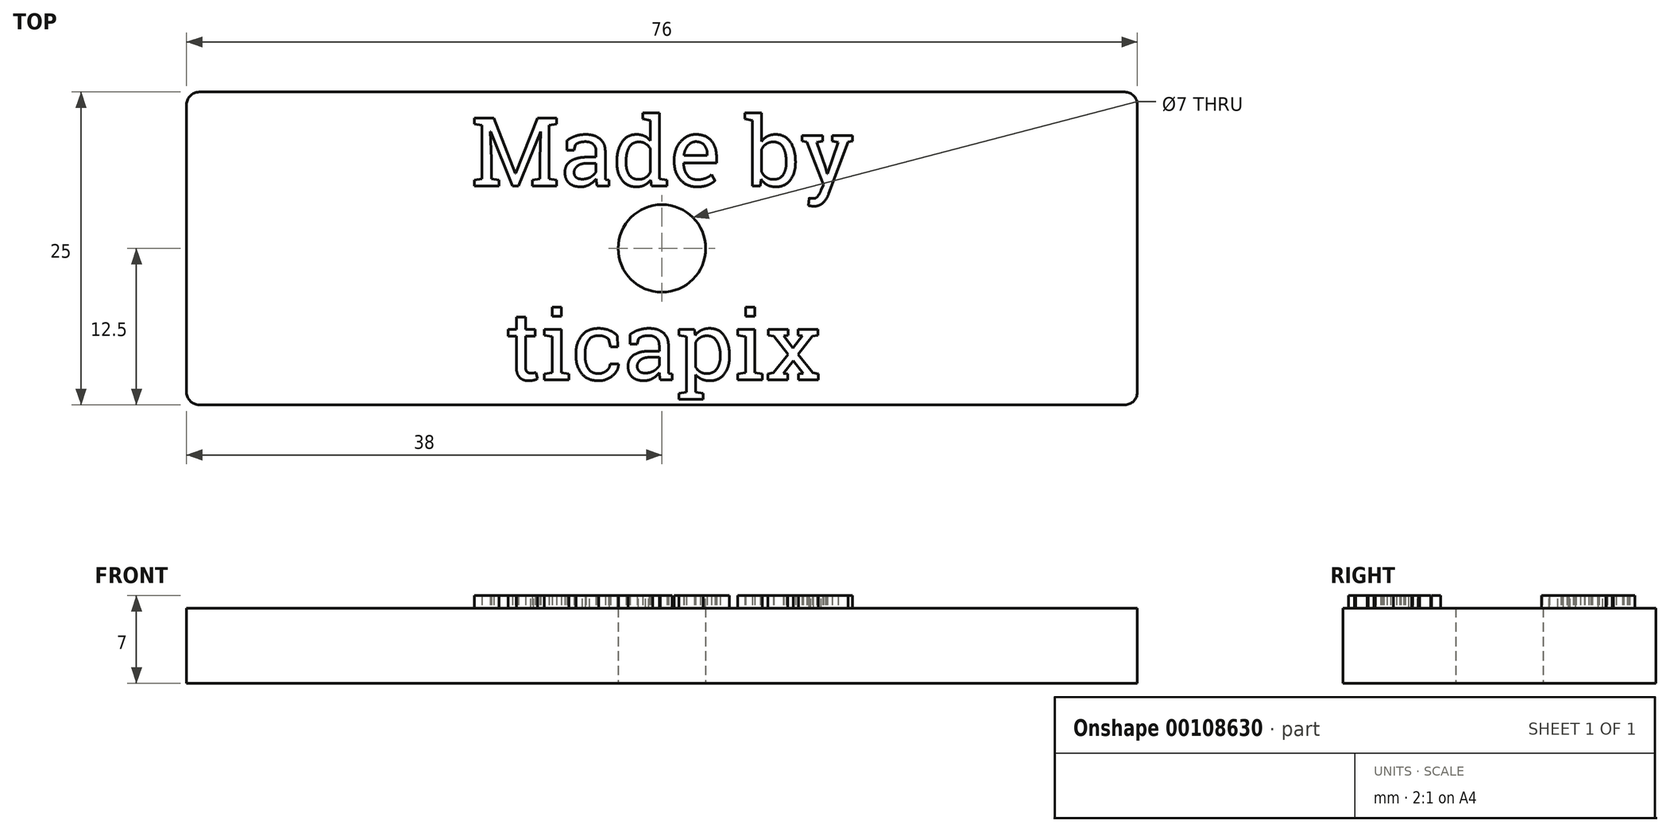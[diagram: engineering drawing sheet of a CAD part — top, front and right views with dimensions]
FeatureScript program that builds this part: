
annotation { "Feature Type Name" : "Feature", "Feature Type Description" : "" }
export const myFeature = defineFeature(function(context is Context, id is Id, definition is map)
    precondition{}
    {
        {
            var Q0;
            Q0=qCreatedBy(makeId("Top.planeOp"),FACE);
            var sketch = newSketch(context, id + "F0", { "sketchPlane" : qUnion([Q0])});
            skLineSegment(sketch, "E0.bottom", {"start": v(-38, 12.5) * mm, "end": v(38, 12.5) * mm});
            skLineSegment(sketch, "E0.top", {"start": v(-38, -12.5) * mm, "end": v(38, -12.5) * mm});
            skLineSegment(sketch, "E0.left", {"start": v(-38, 12.5) * mm, "end": v(-38, -12.5) * mm});
            skLineSegment(sketch, "E0.right", {"start": v(38, 12.5) * mm, "end": v(38, -12.5) * mm});
            skLineSegment(sketch, "E1", {"start": v(-38, -12.5) * mm, "end": v(38, 12.5) * mm, "construction": true});
            skCircle(sketch, "E2", {"center": v(0, 0) * mm, "radius": 3.5 * mm});
            skLineSegment(sketch, "E3", {"start": v(-30, 12.5) * mm, "end": v(-30, -12.5) * mm, "construction": true});
            skLineSegment(sketch, "E4.MirrorCS", {"start": v(30, 12.5) * mm, "end": v(30, -12.5) * mm, "construction": true});
            skSolve(sketch);
        }
        {
            var Q0;
            Q0=qSketchRegion(id+"F0",true);
            extrude(context, id + "F1", {"entities" : qUnion([Q0]), "endBound" : BoundingType.SYMMETRIC, "depth" : 6 * mm});
        }
        {
            var Q0;
            Q0=makeQuery(id+"F1.opExtrude","SWEPT_EDGE",EDGE,{"disambiguationData":[OSD([sQuery(id+"F0.wireOp",EDGE,"E0.bottom"),sQuery(id+"F0.wireOp",EDGE,"E0.right")])]});
            var Q1;
            Q1=makeQuery(id+"F1.opExtrude","SWEPT_EDGE",EDGE,{"disambiguationData":[OSD([sQuery(id+"F0.wireOp",EDGE,"E0.top"),sQuery(id+"F0.wireOp",EDGE,"E0.right")])]});
            var Q2;
            Q2=makeQuery(id+"F1.opExtrude","SWEPT_EDGE",EDGE,{"disambiguationData":[OSD([sQuery(id+"F0.wireOp",EDGE,"E0.top"),sQuery(id+"F0.wireOp",EDGE,"E0.left")])]});
            var Q3;
            Q3=makeQuery(id+"F1.opExtrude","SWEPT_EDGE",EDGE,{"disambiguationData":[OSD([sQuery(id+"F0.wireOp",EDGE,"E0.bottom"),sQuery(id+"F0.wireOp",EDGE,"E0.left")])]});
            fillet(context, id + "F2", {"entities" : qUnion([Q0, Q1, Q2, Q3]), "radius" : 1 * mm, "tangentPropagation" : true, "allowEdgeOverflow" : false});
        }
        {
            var Q0;
            Q0=makeQuery(id+"F1.opExtrude","CAP_FACE",FACE,{"disambiguationData":[OSD([sQuery(id+"F0.wireOp",EDGE,"E0.bottom"),sQuery(id+"F0.wireOp",EDGE,"E0.top"),sQuery(id+"F0.wireOp",EDGE,"E0.left"),sQuery(id+"F0.wireOp",EDGE,"E0.right"),sQuery(id+"F0.wireOp",EDGE,"E2")])],"isStart":false});
            var sketch = newSketch(context, id + "F3", { "sketchPlane" : qUnion([Q0])});
            skText(sketch, "E5", { "text": "ticapix", "fontName": "RobotoSlab-Regular.ttf"});
            skText(sketch, "E6", { "text": "Made by", "fontName": "RobotoSlab-Regular.ttf"});
            skPoint(sketch, "E7", {"position": v(0, 10.5) * mm});
            skPoint(sketch, "E8", {"position": v(0, -5) * mm});
            const initialGuessF3  = {"E5": [-0.01252, -0.0105, 1, 0, 0.0055], "E6": [-0.01525, 0.005, 1, 0, 0.0055]};
            skSetInitialGuess(sketch, initialGuessF3);
            skSolve(sketch);
        }
        {
            var Q0;
            Q0=qSketchRegion(id+"F3",true);
            extrude(context, id + "F4", {"entities" : qUnion([Q0]), "operationType" : NewBodyOperationType.ADD, "depth" : 1 * mm});
        }
    });
